# Revit family: ElectricalFixture_WiringAccessories_Hager_Sollysta_FlatBlankPlate
name_source: partatom
category: Electrical Fixtures
revit_build: Autodesk Revit 2015 (Build: 20160512_1515(x64)
units: mm (PartAtom-declared; Revit-internal decimal feet)

## types (8) — shared parameters
CE Approval = Yes
Default Elevation = 1219.2 mm  [stored 4 ft]
Design Country = China
Expected Life = 25 years
Extrusion From Wall = 3 mm  [stored 0.00984252 ft]
Frequency = 50/60Hz
Gross Weight kg = 0.165
LED Indicator Switch = No
Manufacturer = Hager
Manufacturer Country = United Kingdom
Manufacturer Website = http://www.hager.co.uk
Overall Depth = 28.5 mm
Overall Height = 86 mm  [stored 0.282152 ft]
Packaging Recyclable = Yes
Product Family = DecorativeBlankPlates_BlankPlates
Product Group = WiringAccessories
Product Literature = http://www.hager.co.uk
Product Range = Sollysta
Product URL = http://www.hager.co.uk
Reference Standard = BS 1363-2
Shape = Rectangular
Shipping Weight kg = 0.188
Supply Phase = 1
Switch = Yes
Type = ElectricalFixture
Voltage (Volts) = 230V/240V
zero-valued in all types: Overall Width

## per-type parameters (varying)
| type | Colour | Description | EAN Code | Features | Finish | Material | Name | Overall Length | Product Model Number | Technical Description | Unique Reference |
| WFP1PS | SollystaWhite | SingleBlankPlatePolishedSteel | 5015654742362 | SingleBlankPlatePolishedSteel | Gloss | Hager_PolishedSteel | DecorativeBlankPlate_WFP1PS | 86 mm  [stored 0.282152 ft] | WFP1PS | SingleBlankPlatePolishedSteel | WFP1PS |
| WFP1BS | BrushedSteel | SingleBlankPlateBrushedSteel | 5015654742386 | SingleBlankPlateBrushedSteel | Brushed | Hager_BrushedSteel | DecorativeBlankPlate_WFP1BS | 86 mm  [stored 0.282152 ft] | WFP1BS | SingleBlankPlateBrushedSteel | WFP1BS |
| WFP1PB | PolishedBrass | SingleBlankPlatePolishedBrass | 5015654742409 | SingleBlankPlatePolishedBrass | Polished | Hager_PolishedBrass | DecorativeBlankPlate_WFP1PB | 86 mm  [stored 0.282152 ft] | WFP1PB | SingleBlankPlatePolishedBrass | WFP1PB |
| WFP1BN | BlackNickel | SingleBlankPlateBlackNickel | 5015654742423 | SingleBlankPlateBlackNickel | Polished | Hager_BlackNickel | DecorativeBlankPlate_WFP1BN | 86 mm  [stored 0.282152 ft] | WFP1BN | SingleBlankPlateBlackNickel | WFP1BN |
| WFP2PS | PolishedSteel | TwinBlankPlatePolishedSteel | 5015654742447 | TwinBlankPlatePolishedSteel | Polished | Hager_PolishedSteel | DecorativeBlankPlate_WFP2PS | 146 mm  [stored 0.479003 ft] | WFP1PS | TwinBlankPlatePolishedSteel | WFP1PS |
| WFP2BS | BrushedSteel | TwinBlankPlateBrushedSteel | 5015654742461 | TwinBlankPlateBrushedSteel | Brushed | Hager_BrushedSteel | DecorativeBlankPlate_WFP2BS | 146 mm  [stored 0.479003 ft] | WFP2BS | TwinBlankPlateBrushedSteel | WFP2BS |
| WFP2PB | PolishedBrass | TwinBlankPlatePolishedBrass | 5015654742485 | TwinBlankPlatePolishedBrass | Polished | Hager_PolishedBrass | DecorativeBlankPlate_WFP2PB | 146 mm  [stored 0.479003 ft] | WFP2PB | TwinBlankPlatePolishedBrass | WFP2PB |
| WFP2BN | BlackNickel | TwinBlankPlateBlackNickel | 5015654742508 | TwinBlankPlateBlackNickel | Polished | Hager_BlackNickel | DecorativeBlankPlate_WRP2BN | 146 mm  [stored 0.479003 ft] | WRP2BN | TwinBlankPlateBlackNickel | WRP2BN |

note: [stored X ft] marks values corroborated as IEEE doubles in the binary element streams (Revit-internal decimal feet)

## geometry (parser evidence)
native form markers: Blend x8, Sweep x2
no freeform markers — native parametric forms only
